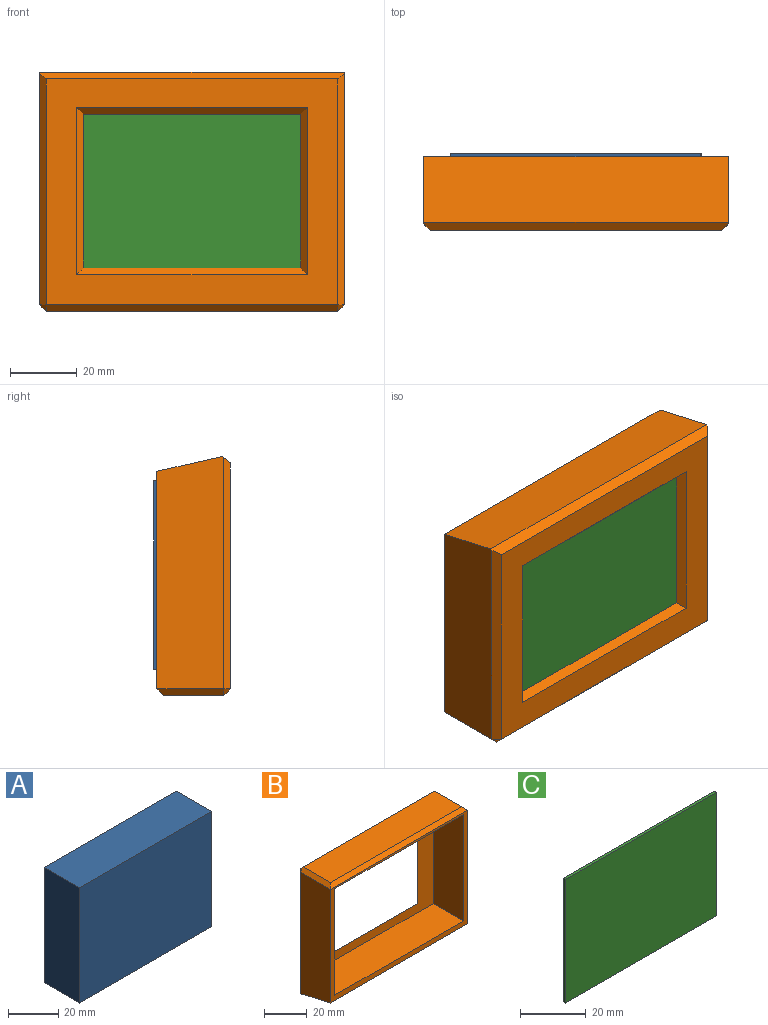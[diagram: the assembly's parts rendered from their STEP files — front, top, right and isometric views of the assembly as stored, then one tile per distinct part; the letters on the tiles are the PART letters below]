
ASSEMBLY  parts=3 mates=2
PART A: 11 faces, bbox 77.7x20x56.3 mm
  f0: plane 56.29x20mm, normal (1,0,0), area 1086.2mm2, adj f1,f3,f4,f5,f6,f7,f8,f9
  f1: plane 74.7x20mm, normal (0,0,1), area 1494.1mm2, adj f0,f2,f4,f5
  f2: plane 56.29x20mm, normal (-1,0,0), area 1125.8mm2, adj f1,f3,f4,f5
  f3: plane 74.7x20mm, normal (0,0,-1), area 1494.1mm2, adj f0,f2,f4,f5
  f4: plane 74.74x56.29mm, normal (0,-1,0), area 4205.1mm2, adj f0,f1,f2,f3
  f5: plane 74.74x56.29mm, normal (0,1,0), area 4205.1mm2, adj f0,f1,f2,f3
  f6: plane 12.1x3.01mm, normal (0,1,0), area 36.3mm2, adj f0,f7,f9,f10
  f7: plane 3.28x3mm, normal (0,0,1), area 9.8mm2, adj f0,f6,f8,f10
  f8: plane 12.1x3.01mm, normal (0,-1,0), area 36.3mm2, adj f0,f7,f9,f10
  f9: plane 3.28x3mm, normal (0,0,-1), area 9.8mm2, adj f0,f6,f8,f10
  f10: plane 12.1x3.28mm, normal (1,0,0), area 39.6mm2, adj f6,f7,f8,f9
PART B: 24 faces, bbox 91x22x71.4 mm
  f0: plane 69.44x20mm, normal (1,0,0), area 1345.4mm2, adj f1,f10,f11,f14,f18
  f1: plane 91x65mm, normal (0,-1,0), area 730mm2, adj f0,f3,f4,f5,f6,f7,f10,f19
  f2: plane 87x18mm, normal (0,0,1), area 1566mm2, adj f13,f17,f18,f19
  f3: plane 69.44x20mm, normal (-1,0,0), area 1345.4mm2, adj f1,f10,f11,f12,f17
  f4: plane 61x20mm, normal (1,0,0), area 1220mm2, adj f1,f5,f7,f9
  f5: plane 85x20mm, normal (0,0,-1), area 1700mm2, adj f1,f4,f6,f9
  f6: plane 61x20mm, normal (-1,0,0), area 1220mm2, adj f1,f5,f7,f9
  f7: plane 85x20mm, normal (0,0,1), area 1700mm2, adj f1,f4,f6,f9
  f8: plane 87x67.49mm, normal (0,1,0), area 2422mm2, adj f11,f12,f13,f14,f20,f21,f22,f23
  f9: plane 85x61mm, normal (0,-1,0), area 2195mm2, adj f4,f5,f6,f7,f20,f21,f22,f23
  f10: plane 91x19.56mm, normal (0,-0.22,-0.98), area 1825mm2, adj f0,f1,f3,f11
  f11: plane 91x2.44mm, normal (0,0.62,-0.78), area 279.4mm2, adj f0,f3,f8,f10,f12,f14
  f12: plane 69.09x2mm, normal (-0.71,0.71,0), area 193.2mm2, adj f3,f8,f11,f15
  f13: plane 87x2mm, normal (0,0.71,0.71), area 246.1mm2, adj f2,f8,f15,f16
  f14: plane 69.09x2mm, normal (0.71,0.71,0), area 193.2mm2, adj f0,f8,f11,f16
  f15: plane 2x2mm, normal (-0.58,0.58,0.58), area 3.5mm2, adj f12,f13,f17
  f16: plane 2x2mm, normal (0.58,0.58,0.58), area 3.5mm2, adj f13,f14,f18
  f17: plane 20x2mm, normal (-0.71,0,0.71), area 53.7mm2, adj f2,f3,f15,f19
  f18: plane 20x2mm, normal (0.71,0,0.71), area 53.7mm2, adj f0,f2,f16,f19
  f19: plane 91x2mm, normal (0,-0.71,0.71), area 251.7mm2, adj f1,f2,f17,f18
  f20: plane 50x2mm, normal (0.71,0.71,0), area 135.8mm2, adj f8,f9,f21,f22
  f21: plane 69x2mm, normal (0,0.71,-0.71), area 189.5mm2, adj f8,f9,f20,f23
  f22: plane 69x2mm, normal (0,0.71,0.71), area 189.5mm2, adj f8,f9,f20,f23
  f23: plane 50x2mm, normal (-0.71,0.71,0), area 135.8mm2, adj f8,f9,f21,f22
PART C: 6 faces, bbox 65x1x46 mm
  f0: plane 65x1mm, normal (0,0,1), area 65mm2, adj f1,f3,f4,f5
  f1: plane 46x1mm, normal (-1,0,0), area 46mm2, adj f0,f2,f4,f5
  f2: plane 65x1mm, normal (0,0,-1), area 65mm2, adj f1,f3,f4,f5
  f3: plane 46x1mm, normal (1,0,0), area 46mm2, adj f0,f2,f4,f5
  f4: plane 65x46mm, normal (0,1,0), area 2990mm2, adj f0,f1,f2,f3
  f5: plane 65x46mm, normal (0,-1,0), area 2990mm2, adj f0,f1,f2,f3
PLACE A rot(axis=(0,1,0),180deg) t=(-60.63,-14.22,-22.78)mm
PLACE B rot(axis=(1,0,0),180deg) t=(-60.91,-37.22,-23.88)mm
PLACE C rot(axis=(0,1,0),180deg) t=(-60.91,-35.22,-23.88)mm
MATE fastened C.f5 <-> B.f9  axis (0,-1,0) through (-60.91,-35.22,-0.88)mm
MATE fastened C.f4 <-> A.f4  axis (0,1,0) through (-60.91,-34.22,-23.88)mm
